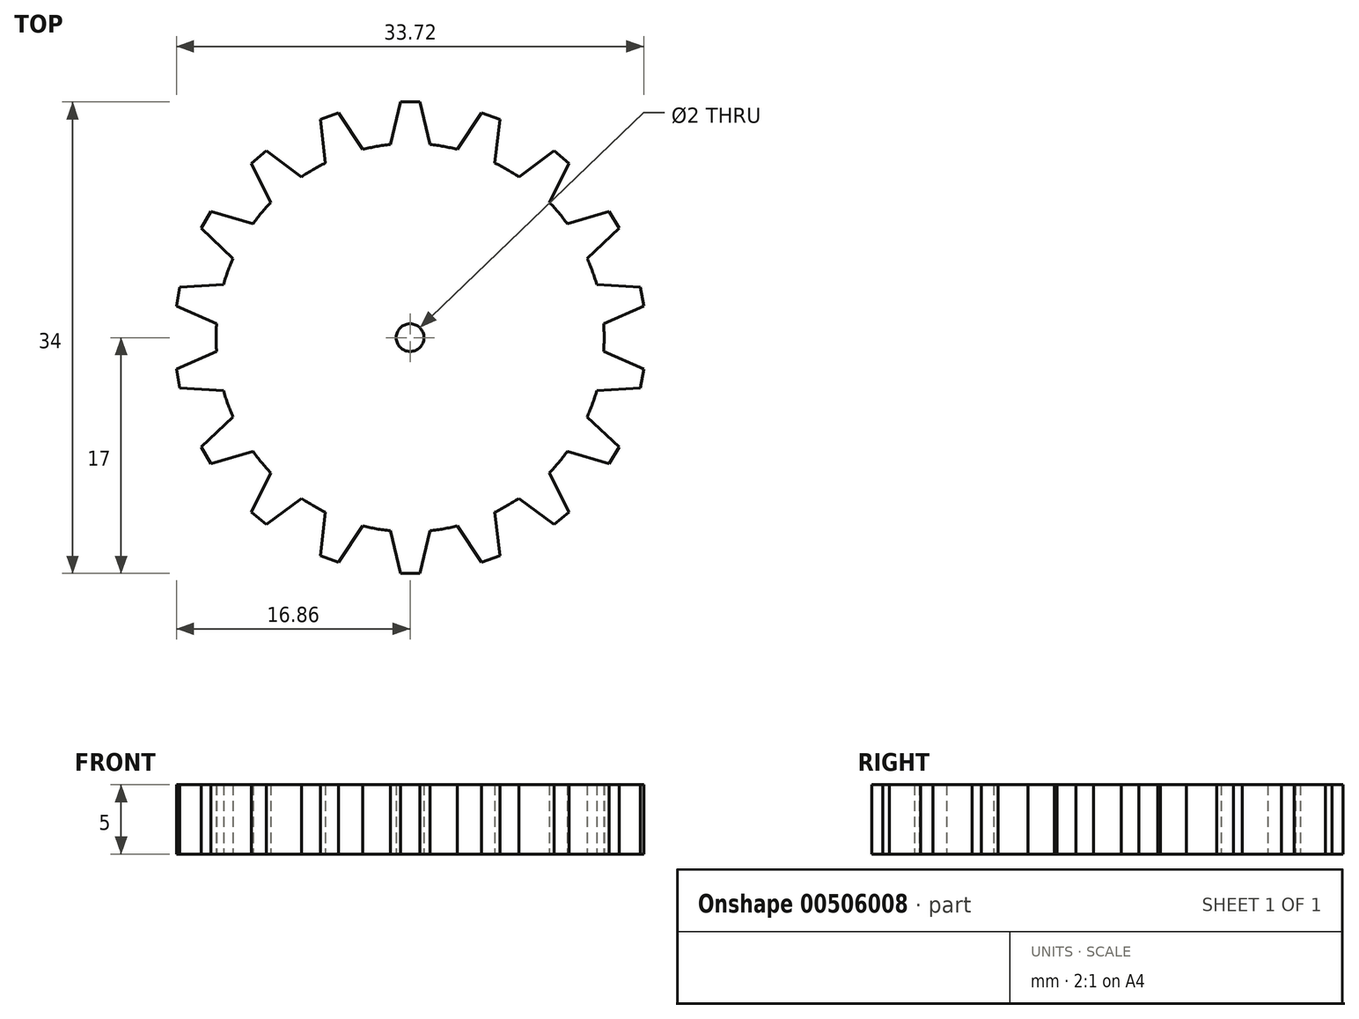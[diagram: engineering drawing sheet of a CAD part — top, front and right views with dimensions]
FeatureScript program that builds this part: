
annotation { "Feature Type Name" : "Feature", "Feature Type Description" : "" }
export const myFeature = defineFeature(function(context is Context, id is Id, definition is map)
    precondition{}
    {
        {
            var Q0;
            Q0=qCreatedBy(makeId("Top.planeOp"),FACE);
            var sketch = newSketch(context, id + "F0", { "sketchPlane" : qUnion([Q0])});
            skCircle(sketch, "E0", {"center": v(0, 0) * mm, "radius": 1 * mm});
            skCircle(sketch, "E1", {"center": v(0, 0) * mm, "radius": 14 * mm});
            skLineSegment(sketch, "E2", {"start": v(0, 17) * mm, "end": v(0.7, 17) * mm});
            skLineSegment(sketch, "E3", {"start": v(0.7, 17) * mm, "end": v(1.44, 13.93) * mm});
            skLineSegment(sketch, "E4.MirrorCS", {"start": v(0, 17) * mm, "end": v(-0.7, 17) * mm});
            skLineSegment(sketch, "E5.MirrorCS", {"start": v(-0.7, 17) * mm, "end": v(-1.44, 13.93) * mm});
            skLineSegment(sketch, "E6.1.0", {"start": v(-5.81, 15.97) * mm, "end": v(-5.16, 16.21) * mm});
            skLineSegment(sketch, "E6.1.1", {"start": v(-5.81, 15.97) * mm, "end": v(-6.47, 15.74) * mm});
            skLineSegment(sketch, "E6.1.2", {"start": v(-6.47, 15.74) * mm, "end": v(-6.11, 12.6) * mm});
            skLineSegment(sketch, "E6.1.3", {"start": v(-5.16, 16.21) * mm, "end": v(-3.41, 13.58) * mm});
            skLineSegment(sketch, "E6.2.0", {"start": v(-10.93, 13.02) * mm, "end": v(-10.4, 13.47) * mm});
            skLineSegment(sketch, "E6.2.1", {"start": v(-10.93, 13.02) * mm, "end": v(-11.46, 12.57) * mm});
            skLineSegment(sketch, "E6.2.2", {"start": v(-11.46, 12.57) * mm, "end": v(-10.05, 9.74) * mm});
            skLineSegment(sketch, "E6.2.3", {"start": v(-10.4, 13.47) * mm, "end": v(-7.85, 11.6) * mm});
            skLineSegment(sketch, "E6.3.0", {"start": v(-14.72, 8.5) * mm, "end": v(-14.37, 9.1) * mm});
            skLineSegment(sketch, "E6.3.1", {"start": v(-14.72, 8.5) * mm, "end": v(-15.07, 7.9) * mm});
            skLineSegment(sketch, "E6.3.2", {"start": v(-15.07, 7.9) * mm, "end": v(-12.78, 5.72) * mm});
            skLineSegment(sketch, "E6.3.3", {"start": v(-14.37, 9.1) * mm, "end": v(-11.34, 8.2) * mm});
            skLineSegment(sketch, "E6.4.0", {"start": v(-16.74, 2.95) * mm, "end": v(-16.62, 3.64) * mm});
            skLineSegment(sketch, "E6.4.1", {"start": v(-16.74, 2.95) * mm, "end": v(-16.86, 2.26) * mm});
            skLineSegment(sketch, "E6.4.2", {"start": v(-16.86, 2.26) * mm, "end": v(-13.96, 1) * mm});
            skLineSegment(sketch, "E6.4.3", {"start": v(-16.62, 3.64) * mm, "end": v(-13.46, 3.83) * mm});
            skLineSegment(sketch, "E6.5.0", {"start": v(-16.74, -2.95) * mm, "end": v(-16.86, -2.26) * mm});
            skLineSegment(sketch, "E6.5.1", {"start": v(-16.74, -2.95) * mm, "end": v(-16.62, -3.64) * mm});
            skLineSegment(sketch, "E6.5.2", {"start": v(-16.62, -3.64) * mm, "end": v(-13.46, -3.83) * mm});
            skLineSegment(sketch, "E6.5.3", {"start": v(-16.86, -2.26) * mm, "end": v(-13.96, -1) * mm});
            skLineSegment(sketch, "E6.6.0", {"start": v(-14.72, -8.5) * mm, "end": v(-15.07, -7.9) * mm});
            skLineSegment(sketch, "E6.6.1", {"start": v(-14.72, -8.5) * mm, "end": v(-14.37, -9.1) * mm});
            skLineSegment(sketch, "E6.6.2", {"start": v(-14.37, -9.1) * mm, "end": v(-11.34, -8.2) * mm});
            skLineSegment(sketch, "E6.6.3", {"start": v(-15.07, -7.9) * mm, "end": v(-12.78, -5.72) * mm});
            skLineSegment(sketch, "E6.7.0", {"start": v(-10.93, -13.02) * mm, "end": v(-11.46, -12.57) * mm});
            skLineSegment(sketch, "E6.7.1", {"start": v(-10.93, -13.02) * mm, "end": v(-10.4, -13.47) * mm});
            skLineSegment(sketch, "E6.7.2", {"start": v(-10.4, -13.47) * mm, "end": v(-7.85, -11.6) * mm});
            skLineSegment(sketch, "E6.7.3", {"start": v(-11.46, -12.57) * mm, "end": v(-10.05, -9.74) * mm});
            skLineSegment(sketch, "E6.8.0", {"start": v(-5.81, -15.97) * mm, "end": v(-6.47, -15.74) * mm});
            skLineSegment(sketch, "E6.8.1", {"start": v(-5.81, -15.97) * mm, "end": v(-5.16, -16.21) * mm});
            skLineSegment(sketch, "E6.8.2", {"start": v(-5.16, -16.21) * mm, "end": v(-3.41, -13.58) * mm});
            skLineSegment(sketch, "E6.8.3", {"start": v(-6.47, -15.74) * mm, "end": v(-6.11, -12.6) * mm});
            skLineSegment(sketch, "E6.9.0", {"start": v(0, -17) * mm, "end": v(-0.7, -17) * mm});
            skLineSegment(sketch, "E6.9.1", {"start": v(0, -17) * mm, "end": v(0.7, -17) * mm});
            skLineSegment(sketch, "E6.9.2", {"start": v(0.7, -17) * mm, "end": v(1.44, -13.93) * mm});
            skLineSegment(sketch, "E6.9.3", {"start": v(-0.7, -17) * mm, "end": v(-1.44, -13.93) * mm});
            skLineSegment(sketch, "E6.10.0", {"start": v(5.81, -15.97) * mm, "end": v(5.16, -16.21) * mm});
            skLineSegment(sketch, "E6.10.1", {"start": v(5.81, -15.97) * mm, "end": v(6.47, -15.74) * mm});
            skLineSegment(sketch, "E6.10.2", {"start": v(6.47, -15.74) * mm, "end": v(6.11, -12.6) * mm});
            skLineSegment(sketch, "E6.10.3", {"start": v(5.16, -16.21) * mm, "end": v(3.41, -13.58) * mm});
            skLineSegment(sketch, "E6.11.0", {"start": v(10.93, -13.02) * mm, "end": v(10.4, -13.47) * mm});
            skLineSegment(sketch, "E6.11.1", {"start": v(10.93, -13.02) * mm, "end": v(11.46, -12.57) * mm});
            skLineSegment(sketch, "E6.11.2", {"start": v(11.46, -12.57) * mm, "end": v(10.05, -9.74) * mm});
            skLineSegment(sketch, "E6.11.3", {"start": v(10.4, -13.47) * mm, "end": v(7.85, -11.6) * mm});
            skLineSegment(sketch, "E6.12.0", {"start": v(14.72, -8.5) * mm, "end": v(14.37, -9.1) * mm});
            skLineSegment(sketch, "E6.12.1", {"start": v(14.72, -8.5) * mm, "end": v(15.07, -7.9) * mm});
            skLineSegment(sketch, "E6.12.2", {"start": v(15.07, -7.9) * mm, "end": v(12.78, -5.72) * mm});
            skLineSegment(sketch, "E6.12.3", {"start": v(14.37, -9.1) * mm, "end": v(11.34, -8.2) * mm});
            skLineSegment(sketch, "E6.13.0", {"start": v(16.74, -2.95) * mm, "end": v(16.62, -3.64) * mm});
            skLineSegment(sketch, "E6.13.1", {"start": v(16.74, -2.95) * mm, "end": v(16.86, -2.26) * mm});
            skLineSegment(sketch, "E6.13.2", {"start": v(16.86, -2.26) * mm, "end": v(13.96, -1) * mm});
            skLineSegment(sketch, "E6.13.3", {"start": v(16.62, -3.64) * mm, "end": v(13.46, -3.83) * mm});
            skLineSegment(sketch, "E6.14.0", {"start": v(16.74, 2.95) * mm, "end": v(16.86, 2.26) * mm});
            skLineSegment(sketch, "E6.14.1", {"start": v(16.74, 2.95) * mm, "end": v(16.62, 3.64) * mm});
            skLineSegment(sketch, "E6.14.2", {"start": v(16.62, 3.64) * mm, "end": v(13.46, 3.83) * mm});
            skLineSegment(sketch, "E6.14.3", {"start": v(16.86, 2.26) * mm, "end": v(13.96, 1) * mm});
            skLineSegment(sketch, "E6.15.0", {"start": v(14.72, 8.5) * mm, "end": v(15.07, 7.9) * mm});
            skLineSegment(sketch, "E6.15.1", {"start": v(14.72, 8.5) * mm, "end": v(14.37, 9.1) * mm});
            skLineSegment(sketch, "E6.15.2", {"start": v(14.37, 9.1) * mm, "end": v(11.34, 8.2) * mm});
            skLineSegment(sketch, "E6.15.3", {"start": v(15.07, 7.9) * mm, "end": v(12.78, 5.72) * mm});
            skLineSegment(sketch, "E6.16.0", {"start": v(10.93, 13.02) * mm, "end": v(11.46, 12.57) * mm});
            skLineSegment(sketch, "E6.16.1", {"start": v(10.93, 13.02) * mm, "end": v(10.4, 13.47) * mm});
            skLineSegment(sketch, "E6.16.2", {"start": v(10.4, 13.47) * mm, "end": v(7.85, 11.6) * mm});
            skLineSegment(sketch, "E6.16.3", {"start": v(11.46, 12.57) * mm, "end": v(10.05, 9.74) * mm});
            skLineSegment(sketch, "E6.17.0", {"start": v(5.81, 15.97) * mm, "end": v(6.47, 15.74) * mm});
            skLineSegment(sketch, "E6.17.1", {"start": v(5.81, 15.97) * mm, "end": v(5.16, 16.21) * mm});
            skLineSegment(sketch, "E6.17.2", {"start": v(5.16, 16.21) * mm, "end": v(3.41, 13.58) * mm});
            skLineSegment(sketch, "E6.17.3", {"start": v(6.47, 15.74) * mm, "end": v(6.11, 12.6) * mm});
            skSolve(sketch);
        }
        {
            var Q0;
            Q0=makeQuery(id+"F0.imprint","IMPRINT",FACE,{"disambiguationData":[TD([[makeQuery(id+"F0.imprint","IMPRINT",EDGE,{"derivedFrom":sQuery(id+"F0.wireOp",EDGE,"E0")}),-1.0]])]});
            var Q1;
            Q1=makeQuery(id+"F0.imprint","IMPRINT",FACE,{"disambiguationData":[TD([[makeQuery(id+"F0.imprint","IMPRINT",EDGE,{"derivedFrom":sQuery(id+"F0.wireOp",EDGE,"E6.12.0")}),-1.0]])]});
            var Q2;
            Q2=makeQuery(id+"F0.imprint","IMPRINT",FACE,{"disambiguationData":[TD([[makeQuery(id+"F0.imprint","IMPRINT",EDGE,{"derivedFrom":sQuery(id+"F0.wireOp",EDGE,"E6.9.0")}),-1.0]])]});
            var Q3;
            Q3=makeQuery(id+"F0.imprint","IMPRINT",FACE,{"disambiguationData":[TD([[makeQuery(id+"F0.imprint","IMPRINT",EDGE,{"derivedFrom":sQuery(id+"F0.wireOp",EDGE,"E6.7.0")}),-1.0]])]});
            var Q4;
            Q4=makeQuery(id+"F0.imprint","IMPRINT",FACE,{"disambiguationData":[TD([[makeQuery(id+"F0.imprint","IMPRINT",EDGE,{"derivedFrom":sQuery(id+"F0.wireOp",EDGE,"E6.11.0")}),-1.0]])]});
            var Q5;
            Q5=makeQuery(id+"F0.imprint","IMPRINT",FACE,{"disambiguationData":[TD([[makeQuery(id+"F0.imprint","IMPRINT",EDGE,{"derivedFrom":sQuery(id+"F0.wireOp",EDGE,"E6.8.0")}),-1.0]])]});
            var Q6;
            Q6=makeQuery(id+"F0.imprint","IMPRINT",FACE,{"disambiguationData":[TD([[makeQuery(id+"F0.imprint","IMPRINT",EDGE,{"derivedFrom":sQuery(id+"F0.wireOp",EDGE,"E6.14.0")}),-1.0]])]});
            var Q7;
            Q7=makeQuery(id+"F0.imprint","IMPRINT",FACE,{"disambiguationData":[TD([[makeQuery(id+"F0.imprint","IMPRINT",EDGE,{"derivedFrom":sQuery(id+"F0.wireOp",EDGE,"E6.13.0")}),-1.0]])]});
            var Q8;
            Q8=makeQuery(id+"F0.imprint","IMPRINT",FACE,{"disambiguationData":[TD([[makeQuery(id+"F0.imprint","IMPRINT",EDGE,{"derivedFrom":sQuery(id+"F0.wireOp",EDGE,"E6.10.0")}),-1.0]])]});
            var Q9;
            Q9=makeQuery(id+"F0.imprint","IMPRINT",FACE,{"disambiguationData":[TD([[makeQuery(id+"F0.imprint","IMPRINT",EDGE,{"derivedFrom":sQuery(id+"F0.wireOp",EDGE,"E2")}),-1.0]])]});
            var Q10;
            Q10=makeQuery(id+"F0.imprint","IMPRINT",FACE,{"disambiguationData":[TD([[makeQuery(id+"F0.imprint","IMPRINT",EDGE,{"derivedFrom":sQuery(id+"F0.wireOp",EDGE,"E6.17.0")}),-1.0]])]});
            var Q11;
            Q11=makeQuery(id+"F0.imprint","IMPRINT",FACE,{"disambiguationData":[TD([[makeQuery(id+"F0.imprint","IMPRINT",EDGE,{"derivedFrom":sQuery(id+"F0.wireOp",EDGE,"E6.15.0")}),-1.0]])]});
            var Q12;
            Q12=makeQuery(id+"F0.imprint","IMPRINT",FACE,{"disambiguationData":[TD([[makeQuery(id+"F0.imprint","IMPRINT",EDGE,{"derivedFrom":sQuery(id+"F0.wireOp",EDGE,"E6.1.0")}),-1.0]])]});
            var Q13;
            Q13=makeQuery(id+"F0.imprint","IMPRINT",FACE,{"disambiguationData":[TD([[makeQuery(id+"F0.imprint","IMPRINT",EDGE,{"derivedFrom":sQuery(id+"F0.wireOp",EDGE,"E6.3.0")}),-1.0]])]});
            var Q14;
            Q14=makeQuery(id+"F0.imprint","IMPRINT",FACE,{"disambiguationData":[TD([[makeQuery(id+"F0.imprint","IMPRINT",EDGE,{"derivedFrom":sQuery(id+"F0.wireOp",EDGE,"E6.16.0")}),-1.0]])]});
            var Q15;
            Q15=makeQuery(id+"F0.imprint","IMPRINT",FACE,{"disambiguationData":[TD([[makeQuery(id+"F0.imprint","IMPRINT",EDGE,{"derivedFrom":sQuery(id+"F0.wireOp",EDGE,"E6.2.0")}),-1.0]])]});
            var Q16;
            Q16=makeQuery(id+"F0.imprint","IMPRINT",FACE,{"disambiguationData":[TD([[makeQuery(id+"F0.imprint","IMPRINT",EDGE,{"derivedFrom":sQuery(id+"F0.wireOp",EDGE,"E6.4.0")}),-1.0]])]});
            var Q17;
            Q17=makeQuery(id+"F0.imprint","IMPRINT",FACE,{"disambiguationData":[TD([[makeQuery(id+"F0.imprint","IMPRINT",EDGE,{"derivedFrom":sQuery(id+"F0.wireOp",EDGE,"E6.5.0")}),-1.0]])]});
            var Q18;
            Q18=makeQuery(id+"F0.imprint","IMPRINT",FACE,{"disambiguationData":[TD([[makeQuery(id+"F0.imprint","IMPRINT",EDGE,{"derivedFrom":sQuery(id+"F0.wireOp",EDGE,"E6.6.0")}),-1.0]])]});
            extrude(context, id + "F1", {"entities" : qUnion([Q0, Q1, Q2, Q3, Q4, Q5, Q6, Q7, Q8, Q9, Q10, Q11, Q12, Q13, Q14, Q15, Q16, Q17, Q18]), "depth" : 5 * mm, "offsetDistance" : 25 * mm});
        }
    });
